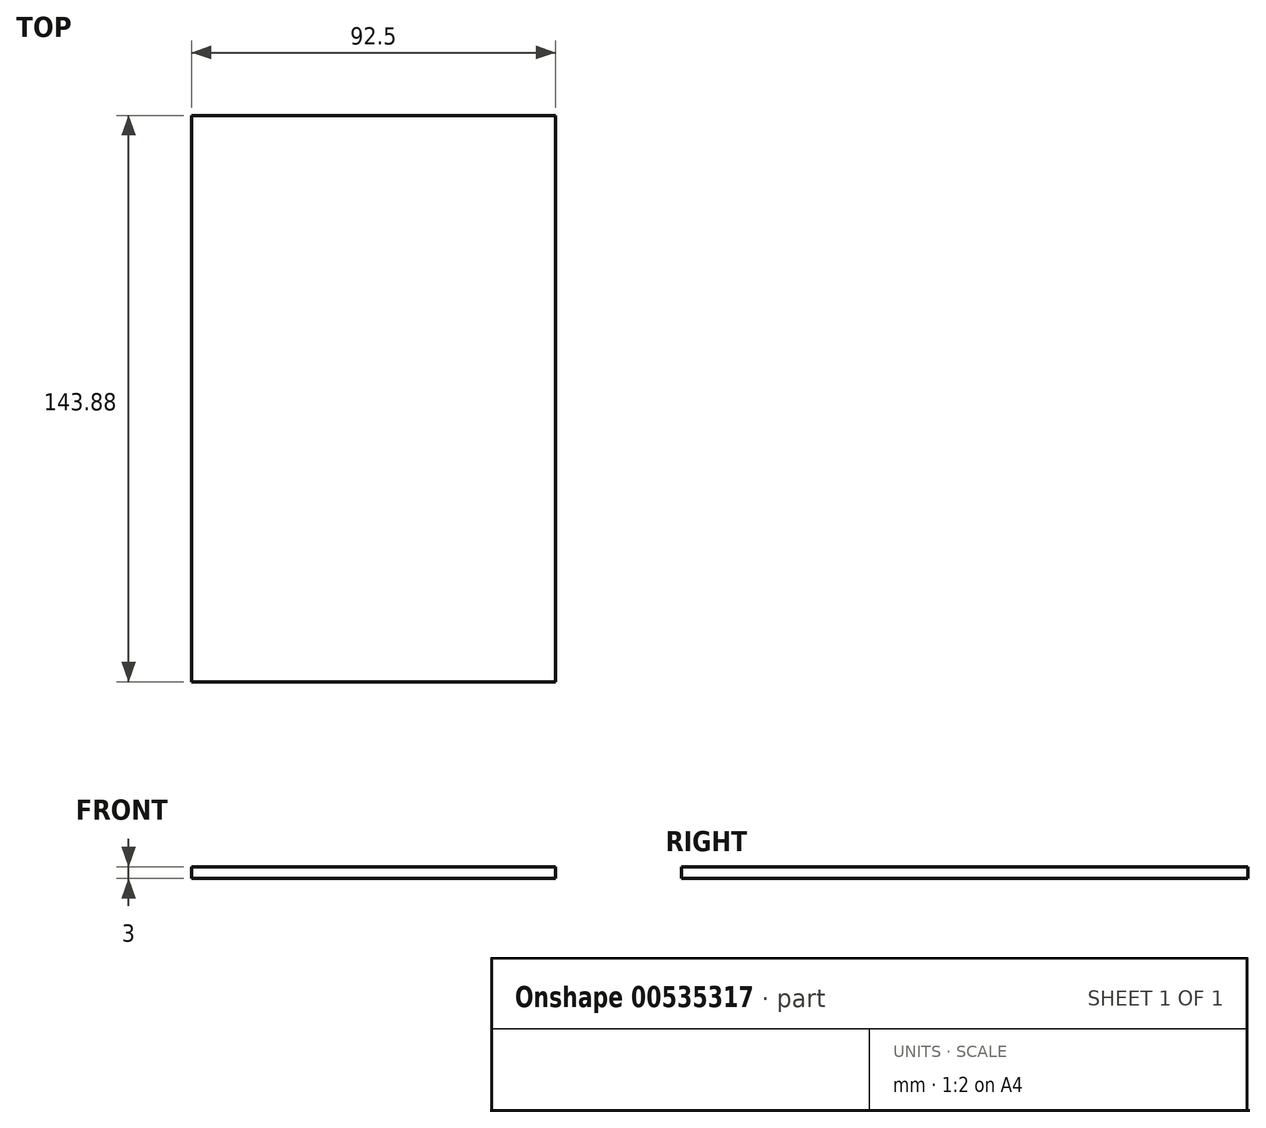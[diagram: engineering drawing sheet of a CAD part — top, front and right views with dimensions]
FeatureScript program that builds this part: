
annotation { "Feature Type Name" : "Feature", "Feature Type Description" : "" }
export const myFeature = defineFeature(function(context is Context, id is Id, definition is map)
    precondition{}
    {
        {
            var Q0;
            Q0=qCreatedBy(makeId("Top.planeOp"),FACE);
            var sketch = newSketch(context, id + "F0", { "sketchPlane" : qUnion([Q0])});
            skLineSegment(sketch, "E0.bottom", {"start": v(-40.88, 55.06) * mm, "end": v(51.62, 55.06) * mm});
            skLineSegment(sketch, "E0.top", {"start": v(-40.88, -88.82) * mm, "end": v(51.62, -88.82) * mm});
            skLineSegment(sketch, "E0.left", {"start": v(-40.88, 55.06) * mm, "end": v(-40.88, -88.82) * mm});
            skLineSegment(sketch, "E0.right", {"start": v(51.62, 55.06) * mm, "end": v(51.62, -88.82) * mm});
            skSolve(sketch);
        }
        {
            var Q0;
            Q0=makeQuery(id+"F0.imprint","IMPRINT",FACE,{"disambiguationData":[TD([[makeQuery(id+"F0.imprint","IMPRINT",EDGE,{"derivedFrom":sQuery(id+"F0.wireOp",EDGE,"E0.bottom")}),-1.0]])]});
            extrude(context, id + "F1", {"entities" : qUnion([Q0]), "depth" : 3 * mm, "offsetDistance" : 25 * mm});
        }
    });
